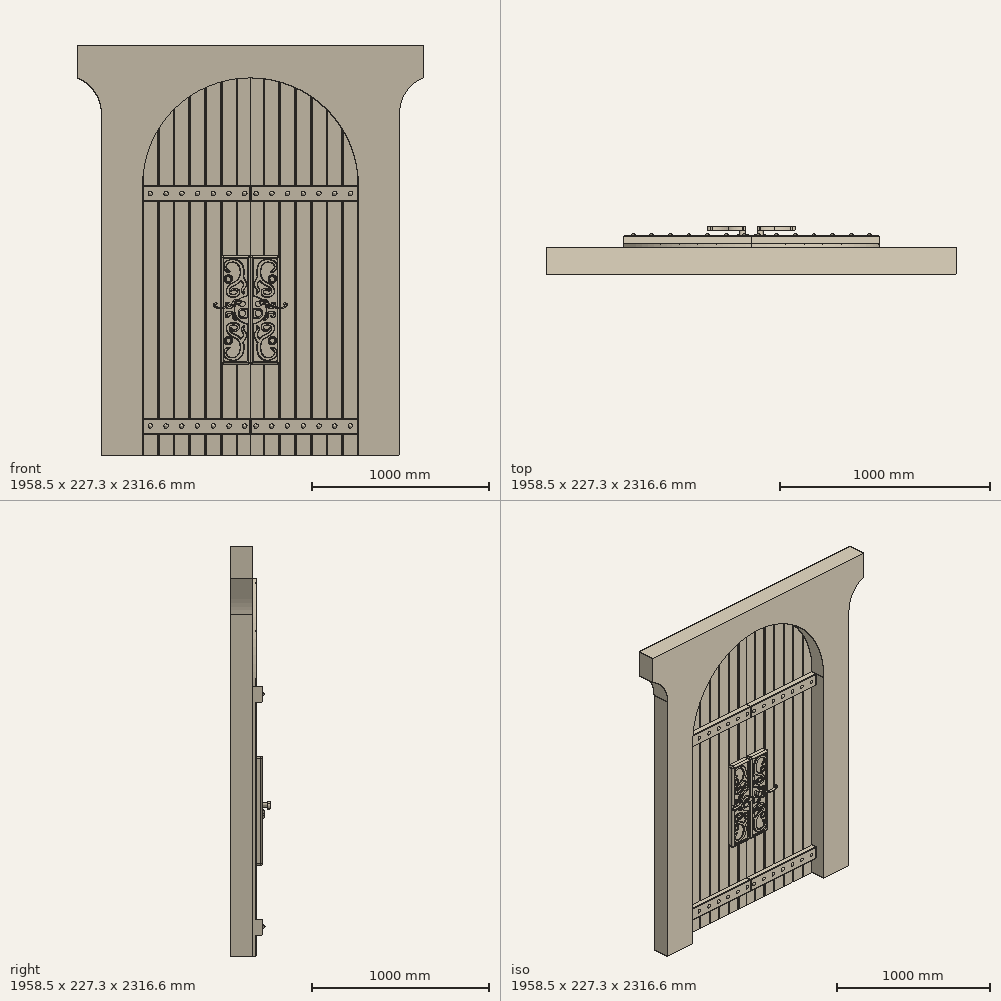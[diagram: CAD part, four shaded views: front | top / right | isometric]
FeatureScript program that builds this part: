
annotation { "Feature Type Name" : "Feature", "Feature Type Description" : "" }
export const myFeature = defineFeature(function(context is Context, id is Id, definition is map)
    precondition{}
    {
        {
            var Q0;
            Q0=qCreatedBy(makeId("Front.planeOp"),FACE);
            var sketch = newSketch(context, id + "F0", { "sketchPlane" : qUnion([Q0])});
            skLineSegment(sketch, "E0.bottom", {"start": v(0, 0) * mm, "end": v(609.6, 0) * mm});
            skLineSegment(sketch, "E0.left", {"start": v(0, 0) * mm, "end": v(0, 1524) * mm});
            skLineSegment(sketch, "E0.right", {"start": v(609.6, 0) * mm, "end": v(609.6, 2133.6) * mm});
            skArc(sketch, "E1", {"start": v(609.6, 2133.6) * mm, "mid": v(178.55, 1955.05) * mm, "end": v(0, 1524) * mm});
            skSolve(sketch);
        }
        {
            var Q0;
            Q0 = qSketchRegion(id + "F0", true);
            extrude(context, id + "F1", {"entities" : qUnion([Q0]), "depth" : 38.1 * mm, "offsetDistance" : 25.4 * mm});
        }
        {
            var Q0;
            Q0=makeQuery(id+"F1.opExtrude","SWEPT_FACE",FACE,{"disambiguationData":[OSD([sQuery(id+"F0.wireOp",EDGE,"E0.bottom")])]});
            var sketch = newSketch(context, id + "F2", { "sketchPlane" : qUnion([Q0])});
            skLineSegment(sketch, "E2.bottom", {"start": v(5.08, 38.1) * mm, "end": v(83.82, 38.1) * mm});
            skLineSegment(sketch, "E2.top", {"start": v(5.08, 0) * mm, "end": v(83.82, 0) * mm});
            skLineSegment(sketch, "E2.left", {"start": v(0, 33.02) * mm, "end": v(0, 5.08) * mm});
            skPoint(sketch, "E3.visualSharp", {"position": v(0, 38.1) * mm});
            skArc(sketch, "E3.filletArc", {"start": v(5.08, 38.1) * mm, "mid": v(1.49, 36.61) * mm, "end": v(0, 33.02) * mm});
            skPoint(sketch, "E4.visualSharp", {"position": v(0, 0) * mm});
            skArc(sketch, "E4.filletArc", {"start": v(0, 5.08) * mm, "mid": v(1.49, 1.49) * mm, "end": v(5.08, 0) * mm});
            skPoint(sketch, "E5.visualSharp", {"position": v(88.9, 0) * mm});
            skArc(sketch, "E5.filletArc", {"start": v(83.82, 0) * mm, "mid": v(87.41, 1.49) * mm, "end": v(88.9, 5.08) * mm});
            skPoint(sketch, "E6.visualSharp", {"position": v(88.9, 38.1) * mm});
            skArc(sketch, "E6.filletArc", {"start": v(88.9, 33.02) * mm, "mid": v(87.41, 36.61) * mm, "end": v(83.82, 38.1) * mm});
            skArc(sketch, "E7.1.0.0", {"start": v(177.8, 33.02) * mm, "mid": v(176.31, 36.61) * mm, "end": v(172.72, 38.1) * mm});
            skLineSegment(sketch, "E7.1.0.1", {"start": v(93.98, 38.1) * mm, "end": v(172.72, 38.1) * mm});
            skArc(sketch, "E7.1.0.3", {"start": v(172.72, 0) * mm, "mid": v(176.31, 1.49) * mm, "end": v(177.8, 5.08) * mm});
            skArc(sketch, "E7.1.0.4", {"start": v(88.9, 5.08) * mm, "mid": v(90.39, 1.49) * mm, "end": v(93.98, 0) * mm});
            skLineSegment(sketch, "E7.1.0.5", {"start": v(93.98, 0) * mm, "end": v(172.72, 0) * mm});
            skArc(sketch, "E7.1.0.7", {"start": v(93.98, 38.1) * mm, "mid": v(90.39, 36.61) * mm, "end": v(88.9, 33.02) * mm});
            skArc(sketch, "E7.2.0.0", {"start": v(266.7, 33.02) * mm, "mid": v(265.21, 36.61) * mm, "end": v(261.62, 38.1) * mm});
            skLineSegment(sketch, "E7.2.0.1", {"start": v(182.88, 38.1) * mm, "end": v(261.62, 38.1) * mm});
            skArc(sketch, "E7.2.0.3", {"start": v(261.62, 0) * mm, "mid": v(265.21, 1.49) * mm, "end": v(266.7, 5.08) * mm});
            skArc(sketch, "E7.2.0.4", {"start": v(177.8, 5.08) * mm, "mid": v(179.29, 1.49) * mm, "end": v(182.88, 0) * mm});
            skLineSegment(sketch, "E7.2.0.5", {"start": v(182.88, 0) * mm, "end": v(261.62, 0) * mm});
            skArc(sketch, "E7.2.0.7", {"start": v(182.88, 38.1) * mm, "mid": v(179.29, 36.61) * mm, "end": v(177.8, 33.02) * mm});
            skLineSegment(sketch, "E7.direction1", {"start": v(83.82, 33.02) * mm, "end": v(172.72, 33.02) * mm, "construction": true});
            skArc(sketch, "E8.0.3.0", {"start": v(355.6, 33.02) * mm, "mid": v(354.11, 36.61) * mm, "end": v(350.52, 38.1) * mm});
            skLineSegment(sketch, "E8.4.3.0", {"start": v(271.78, 38.1) * mm, "end": v(350.52, 38.1) * mm});
            skArc(sketch, "E8.10.3.0", {"start": v(350.52, 0) * mm, "mid": v(354.11, 1.49) * mm, "end": v(355.6, 5.08) * mm});
            skArc(sketch, "E8.14.3.0", {"start": v(266.7, 5.08) * mm, "mid": v(268.19, 1.49) * mm, "end": v(271.78, 0) * mm});
            skLineSegment(sketch, "E8.18.3.0", {"start": v(271.78, 0) * mm, "end": v(350.52, 0) * mm});
            skArc(sketch, "E8.24.3.0", {"start": v(271.78, 38.1) * mm, "mid": v(268.19, 36.61) * mm, "end": v(266.7, 33.02) * mm});
            skArc(sketch, "E8.0.4.0", {"start": v(444.5, 33.02) * mm, "mid": v(443.01, 36.61) * mm, "end": v(439.42, 38.1) * mm});
            skLineSegment(sketch, "E8.4.4.0", {"start": v(360.68, 38.1) * mm, "end": v(439.42, 38.1) * mm});
            skArc(sketch, "E8.10.4.0", {"start": v(439.42, 0) * mm, "mid": v(443.01, 1.49) * mm, "end": v(444.5, 5.08) * mm});
            skArc(sketch, "E8.14.4.0", {"start": v(355.6, 5.08) * mm, "mid": v(357.09, 1.49) * mm, "end": v(360.68, 0) * mm});
            skLineSegment(sketch, "E8.18.4.0", {"start": v(360.68, 0) * mm, "end": v(439.42, 0) * mm});
            skArc(sketch, "E8.24.4.0", {"start": v(360.68, 38.1) * mm, "mid": v(357.09, 36.61) * mm, "end": v(355.6, 33.02) * mm});
            skArc(sketch, "E8.0.5.0", {"start": v(533.4, 33.02) * mm, "mid": v(531.91, 36.61) * mm, "end": v(528.32, 38.1) * mm});
            skLineSegment(sketch, "E8.4.5.0", {"start": v(449.58, 38.1) * mm, "end": v(528.32, 38.1) * mm});
            skArc(sketch, "E8.10.5.0", {"start": v(528.32, 0) * mm, "mid": v(531.91, 1.49) * mm, "end": v(533.4, 5.08) * mm});
            skArc(sketch, "E8.14.5.0", {"start": v(444.5, 5.08) * mm, "mid": v(445.99, 1.49) * mm, "end": v(449.58, 0) * mm});
            skLineSegment(sketch, "E8.18.5.0", {"start": v(449.58, 0) * mm, "end": v(528.32, 0) * mm});
            skArc(sketch, "E8.24.5.0", {"start": v(449.58, 38.1) * mm, "mid": v(445.99, 36.61) * mm, "end": v(444.5, 33.02) * mm});
            skArc(sketch, "E8.0.6.0", {"start": v(622.3, 33.02) * mm, "mid": v(620.81, 36.61) * mm, "end": v(617.22, 38.1) * mm});
            skLineSegment(sketch, "E8.4.6.0", {"start": v(538.48, 38.1) * mm, "end": v(617.22, 38.1) * mm});
            skLineSegment(sketch, "E8.7.6.0", {"start": v(622.3, 33.02) * mm, "end": v(622.3, 5.08) * mm});
            skArc(sketch, "E8.10.6.0", {"start": v(617.22, 0) * mm, "mid": v(620.81, 1.49) * mm, "end": v(622.3, 5.08) * mm});
            skArc(sketch, "E8.14.6.0", {"start": v(533.4, 5.08) * mm, "mid": v(534.89, 1.49) * mm, "end": v(538.48, 0) * mm});
            skLineSegment(sketch, "E8.18.6.0", {"start": v(538.48, 0) * mm, "end": v(617.22, 0) * mm});
            skArc(sketch, "E8.24.6.0", {"start": v(538.48, 38.1) * mm, "mid": v(534.89, 36.61) * mm, "end": v(533.4, 33.02) * mm});
            skLineSegment(sketch, "E9.bottom", {"start": v(-46.54, 115.07) * mm, "end": v(633.76, 115.07) * mm});
            skLineSegment(sketch, "E9.top", {"start": v(-46.54, -46) * mm, "end": v(633.76, -46) * mm});
            skLineSegment(sketch, "E9.left", {"start": v(-46.54, 115.07) * mm, "end": v(-46.54, -46) * mm});
            skLineSegment(sketch, "E9.right", {"start": v(633.76, 115.07) * mm, "end": v(633.76, -46) * mm});
            skSolve(sketch);
        }
        {
            var Q0;
            Q0 = qSketchRegion(id + "F2", true);
            extrude(context, id + "F3", {"entities" : qUnion([Q0]), "operationType" : NewBodyOperationType.REMOVE, "oppositeDirection" : true, "depth" : 2153.92 * mm, "offsetDistance" : 25.4 * mm});
        }
        {
            var Q0;
            Q0=qCreatedBy(makeId("Front.planeOp"),FACE);
            cPlane(context, id + "F4", {"entities" : qUnion([Q0]), "cplaneType" : CPlaneType.OFFSET, "offset" : 19.05 * mm, "width" : 152.4 * mm, "height" : 152.4 * mm});
        }
        {
            var Q0;
            Q0=qCreatedBy(id+"F4.planeOp",FACE);
            var sketch = newSketch(context, id + "F5", { "sketchPlane" : qUnion([Q0])});
            skLineSegment(sketch, "E10.bottom", {"start": v(0, 1524) * mm, "end": v(609.6, 1524) * mm});
            skLineSegment(sketch, "E10.top", {"start": v(0, 1435.1) * mm, "end": v(609.6, 1435.1) * mm});
            skLineSegment(sketch, "E10.left", {"start": v(0, 1524) * mm, "end": v(0, 1435.1) * mm});
            skLineSegment(sketch, "E10.right", {"start": v(609.6, 1524) * mm, "end": v(609.6, 1435.1) * mm});
            skLineSegment(sketch, "E11.bottom", {"start": v(0, 120.72) * mm, "end": v(609.6, 120.72) * mm});
            skLineSegment(sketch, "E11.top", {"start": v(0, 209.62) * mm, "end": v(609.6, 209.62) * mm});
            skLineSegment(sketch, "E11.left", {"start": v(0, 120.72) * mm, "end": v(0, 209.62) * mm});
            skLineSegment(sketch, "E11.right", {"start": v(609.6, 120.72) * mm, "end": v(609.6, 209.62) * mm});
            skSolve(sketch);
        }
        {
            var Q0;
            Q0 = qSketchRegion(id + "F5", true);
            extrude(context, id + "F6", {"entities" : qUnion([Q0]), "operationType" : NewBodyOperationType.ADD, "depth" : 57.15 * mm, "offsetDistance" : 25.4 * mm, "hasSecondDirection" : true, "secondDirectionOppositeDirection" : true, "secondDirectionDepth" : 57.15 * mm});
        }
        {
            var Q0;
            Q0=makeQuery(id+"F6.opExtrude","CAP_EDGE",EDGE,{"disambiguationData":[OSD([sQuery(id+"F5.wireOp",EDGE,"E10.bottom")])],"isStart":false});
            var Q1;
            Q1=makeQuery(id+"F6.opExtrude","CAP_EDGE",EDGE,{"disambiguationData":[OSD([sQuery(id+"F5.wireOp",EDGE,"E10.top")])],"isStart":false});
            var Q2;
            Q2=makeQuery(id+"F6.opExtrude","CAP_EDGE",EDGE,{"disambiguationData":[OSD([sQuery(id+"F5.wireOp",EDGE,"E10.left")])],"isStart":false});
            var Q3;
            Q3=makeQuery(id+"F6.opExtrude","CAP_EDGE",EDGE,{"disambiguationData":[OSD([sQuery(id+"F5.wireOp",EDGE,"E10.right")])],"isStart":false});
            var Q4;
            Q4=makeQuery(id+"F6.opExtrude","CAP_FACE",FACE,{"disambiguationData":[OSD([sQuery(id+"F5.wireOp",EDGE,"E11.bottom"),sQuery(id+"F5.wireOp",EDGE,"E11.top"),sQuery(id+"F5.wireOp",EDGE,"E11.left"),sQuery(id+"F5.wireOp",EDGE,"E11.right")])],"isStart":false});
            var Q5;
            Q5=makeQuery(id+"F6.opExtrude","CAP_FACE",FACE,{"disambiguationData":[OSD([sQuery(id+"F5.wireOp",EDGE,"E10.bottom"),sQuery(id+"F5.wireOp",EDGE,"E10.top"),sQuery(id+"F5.wireOp",EDGE,"E10.left"),sQuery(id+"F5.wireOp",EDGE,"E10.right")])],"isStart":true});
            var Q6;
            Q6=makeQuery(id+"F6.opExtrude","CAP_FACE",FACE,{"disambiguationData":[OSD([sQuery(id+"F5.wireOp",EDGE,"E11.bottom"),sQuery(id+"F5.wireOp",EDGE,"E11.top"),sQuery(id+"F5.wireOp",EDGE,"E11.left"),sQuery(id+"F5.wireOp",EDGE,"E11.right")])],"isStart":true});
            fillet(context, id + "F7", {"entities" : qUnion([Q0, Q1, Q2, Q3, Q4, Q5, Q6]), "radius" : 5.08 * mm, "tangentPropagation" : true, "allowEdgeOverflow" : false});
        }
        {
            var Q0;
            Q0=qCreatedBy(id+"F4.planeOp",FACE);
            var sketch = newSketch(context, id + "F8", { "sketchPlane" : qUnion([Q0])});
            skLineSegment(sketch, "E12.bottom", {"start": v(609.6, 1130.3) * mm, "end": v(444.5, 1130.3) * mm});
            skLineSegment(sketch, "E12.top", {"start": v(609.6, 514.42) * mm, "end": v(444.5, 514.42) * mm});
            skLineSegment(sketch, "E12.left", {"start": v(609.6, 1130.3) * mm, "end": v(609.6, 514.42) * mm});
            skLineSegment(sketch, "E12.right", {"start": v(444.5, 1130.3) * mm, "end": v(444.5, 514.42) * mm});
            skSolve(sketch);
        }
        {
            var Q0;
            Q0 = qSketchRegion(id + "F8", true);
            extrude(context, id + "F9", {"entities" : qUnion([Q0]), "operationType" : NewBodyOperationType.ADD, "depth" : 57.15 * mm, "offsetDistance" : 25.4 * mm, "hasSecondDirection" : true, "secondDirectionOppositeDirection" : true, "secondDirectionDepth" : 57.15 * mm});
        }
        {
            var Q0;
            {var subQ0=sQuery(id+"F8.wireOp",EDGE,"E12.left");var subQ1=sQuery(id+"F8.wireOp",EDGE,"E12.bottom");var subQ2=sQuery(id+"F0.wireOp",EDGE,"E0.right");Q0=makeQuery(id+"F9.boolean.opBoolean","SPLIT",EDGE,{"disambiguationData":[TD([makeQuery(id+"F1.opExtrude","CAP_FACE",FACE,{"disambiguationData":[OSD([sQuery(id+"F0.wireOp",EDGE,"E0.bottom"),sQuery(id+"F0.wireOp",EDGE,"E0.left"),subQ2,sQuery(id+"F0.wireOp",EDGE,"E1")])],"isStart":false})])],"derivedFrom":makeQuery(id+"F9.opExtrude","SWEPT_EDGE",EDGE,{"disambiguationData":[OSD([subQ1,subQ0])]})});}
            var Q1;
            {var subQ0=sQuery(id+"F8.wireOp",EDGE,"E12.right");var subQ1=sQuery(id+"F8.wireOp",EDGE,"E12.bottom");Q1=makeQuery(id+"F9.boolean.opBoolean","SPLIT",EDGE,{"disambiguationData":[TD([makeQuery(id+"F3.boolean.opBoolean","COPY",FACE,{"derivedFrom":makeQuery(id+"F3.opExtrude","SWEPT_FACE",FACE,{"disambiguationData":[OSD([sQuery(id+"F2.wireOp",EDGE,"E8.0.4.0")])]})})])],"derivedFrom":makeQuery(id+"F9.opExtrude","SWEPT_EDGE",EDGE,{"disambiguationData":[OSD([subQ1,subQ0])]})});}
            var Q2;
            {var subQ0=sQuery(id+"F0.wireOp",EDGE,"E0.right");var subQ1=sQuery(id+"F8.wireOp",EDGE,"E12.bottom");var subQ2=sQuery(id+"F8.wireOp",EDGE,"E12.left");Q2=makeQuery(id+"F9.boolean.opBoolean","SPLIT",EDGE,{"disambiguationData":[TD([makeQuery(id+"F1.opExtrude","CAP_FACE",FACE,{"disambiguationData":[OSD([sQuery(id+"F0.wireOp",EDGE,"E0.bottom"),sQuery(id+"F0.wireOp",EDGE,"E0.left"),subQ0,sQuery(id+"F0.wireOp",EDGE,"E1")])],"isStart":true})])],"derivedFrom":makeQuery(id+"F9.opExtrude","SWEPT_EDGE",EDGE,{"disambiguationData":[OSD([subQ1,subQ2])]})});}
            var Q3;
            {var subQ0=sQuery(id+"F8.wireOp",EDGE,"E12.right");var subQ1=sQuery(id+"F8.wireOp",EDGE,"E12.bottom");Q3=makeQuery(id+"F9.boolean.opBoolean","SPLIT",EDGE,{"disambiguationData":[TD([makeQuery(id+"F3.boolean.opBoolean","COPY",FACE,{"derivedFrom":makeQuery(id+"F3.opExtrude","SWEPT_FACE",FACE,{"disambiguationData":[OSD([sQuery(id+"F2.wireOp",EDGE,"E8.10.4.0")])]})})])],"derivedFrom":makeQuery(id+"F9.opExtrude","SWEPT_EDGE",EDGE,{"disambiguationData":[OSD([subQ1,subQ0])]})});}
            var Q4;
            {var subQ0=sQuery(id+"F8.wireOp",EDGE,"E12.top");var subQ1=sQuery(id+"F8.wireOp",EDGE,"E12.right");Q4=makeQuery(id+"F9.boolean.opBoolean","SPLIT",EDGE,{"disambiguationData":[TD([makeQuery(id+"F3.boolean.opBoolean","COPY",FACE,{"derivedFrom":makeQuery(id+"F3.opExtrude","SWEPT_FACE",FACE,{"disambiguationData":[OSD([sQuery(id+"F2.wireOp",EDGE,"E8.10.4.0")])]})})])],"derivedFrom":makeQuery(id+"F9.opExtrude","SWEPT_EDGE",EDGE,{"disambiguationData":[OSD([subQ0,subQ1])]})});}
            var Q5;
            {var subQ0=sQuery(id+"F0.wireOp",EDGE,"E0.right");var subQ1=sQuery(id+"F8.wireOp",EDGE,"E12.top");var subQ2=sQuery(id+"F8.wireOp",EDGE,"E12.left");Q5=makeQuery(id+"F9.boolean.opBoolean","SPLIT",EDGE,{"disambiguationData":[TD([makeQuery(id+"F1.opExtrude","CAP_FACE",FACE,{"disambiguationData":[OSD([sQuery(id+"F0.wireOp",EDGE,"E0.bottom"),sQuery(id+"F0.wireOp",EDGE,"E0.left"),subQ0,sQuery(id+"F0.wireOp",EDGE,"E1")])],"isStart":true})])],"derivedFrom":makeQuery(id+"F9.opExtrude","SWEPT_EDGE",EDGE,{"disambiguationData":[OSD([subQ1,subQ2])]})});}
            var Q6;
            {var subQ0=sQuery(id+"F8.wireOp",EDGE,"E12.left");var subQ1=sQuery(id+"F8.wireOp",EDGE,"E12.top");var subQ2=sQuery(id+"F0.wireOp",EDGE,"E0.right");Q6=makeQuery(id+"F9.boolean.opBoolean","SPLIT",EDGE,{"disambiguationData":[TD([makeQuery(id+"F1.opExtrude","CAP_FACE",FACE,{"disambiguationData":[OSD([sQuery(id+"F0.wireOp",EDGE,"E0.bottom"),sQuery(id+"F0.wireOp",EDGE,"E0.left"),subQ2,sQuery(id+"F0.wireOp",EDGE,"E1")])],"isStart":false})])],"derivedFrom":makeQuery(id+"F9.opExtrude","SWEPT_EDGE",EDGE,{"disambiguationData":[OSD([subQ1,subQ0])]})});}
            var Q7;
            {var subQ0=sQuery(id+"F8.wireOp",EDGE,"E12.right");var subQ1=sQuery(id+"F8.wireOp",EDGE,"E12.top");Q7=makeQuery(id+"F9.boolean.opBoolean","SPLIT",EDGE,{"disambiguationData":[TD([makeQuery(id+"F3.boolean.opBoolean","COPY",FACE,{"derivedFrom":makeQuery(id+"F3.opExtrude","SWEPT_FACE",FACE,{"disambiguationData":[OSD([sQuery(id+"F2.wireOp",EDGE,"E8.0.4.0")])]})})])],"derivedFrom":makeQuery(id+"F9.opExtrude","SWEPT_EDGE",EDGE,{"disambiguationData":[OSD([subQ1,subQ0])]})});}
            var Q8;
            Q8=makeQuery(id+"F9.opExtrude","CAP_FACE",FACE,{"disambiguationData":[OSD([sQuery(id+"F8.wireOp",EDGE,"E12.bottom"),sQuery(id+"F8.wireOp",EDGE,"E12.top"),sQuery(id+"F8.wireOp",EDGE,"E12.left"),sQuery(id+"F8.wireOp",EDGE,"E12.right")])],"isStart":false});
            var Q9;
            Q9=makeQuery(id+"F9.opExtrude","CAP_FACE",FACE,{"disambiguationData":[OSD([sQuery(id+"F8.wireOp",EDGE,"E12.bottom"),sQuery(id+"F8.wireOp",EDGE,"E12.top"),sQuery(id+"F8.wireOp",EDGE,"E12.left"),sQuery(id+"F8.wireOp",EDGE,"E12.right")])],"isStart":true});
            fillet(context, id + "F10", {"entities" : qUnion([Q0, Q1, Q2, Q3, Q4, Q5, Q6, Q7, Q8, Q9]), "radius" : 12.7 * mm, "tangentPropagation" : true, "allowEdgeOverflow" : false});
        }
        {
            var Q0;
            Q0=makeQuery(id+"F9.opExtrude","CAP_FACE",FACE,{"disambiguationData":[OSD([sQuery(id+"F8.wireOp",EDGE,"E12.bottom"),sQuery(id+"F8.wireOp",EDGE,"E12.top"),sQuery(id+"F8.wireOp",EDGE,"E12.left"),sQuery(id+"F8.wireOp",EDGE,"E12.right")])],"isStart":false});
            var sketch = newSketch(context, id + "F11", { "sketchPlane" : qUnion([Q0])});
            skArc(sketch, "E13", {"start": v(586.01, 746.94) * mm, "mid": v(520.7, 822.36) * mm, "end": v(586.01, 897.78) * mm});
            skLineSegment(sketch, "E14", {"start": v(596.9, 734.37) * mm, "end": v(596.9, 539.82) * mm});
            skLineSegment(sketch, "E15", {"start": v(584.2, 527.12) * mm, "end": v(469.9, 527.12) * mm});
            skLineSegment(sketch, "E16", {"start": v(457.2, 539.82) * mm, "end": v(457.2, 1104.9) * mm});
            skLineSegment(sketch, "E17", {"start": v(469.9, 1117.6) * mm, "end": v(584.2, 1117.6) * mm});
            skLineSegment(sketch, "E18", {"start": v(596.9, 1104.9) * mm, "end": v(596.9, 910.35) * mm});
            skPoint(sketch, "E19.visualSharp", {"position": v(596.9, 1117.6) * mm});
            skArc(sketch, "E19.filletArc", {"start": v(596.9, 1104.9) * mm, "mid": v(593.18, 1113.88) * mm, "end": v(584.2, 1117.6) * mm});
            skPoint(sketch, "E20.visualSharp", {"position": v(457.2, 1117.6) * mm});
            skArc(sketch, "E20.filletArc", {"start": v(469.9, 1117.6) * mm, "mid": v(460.92, 1113.88) * mm, "end": v(457.2, 1104.9) * mm});
            skPoint(sketch, "E21.visualSharp", {"position": v(457.2, 527.12) * mm});
            skArc(sketch, "E21.filletArc", {"start": v(457.2, 539.82) * mm, "mid": v(460.92, 530.84) * mm, "end": v(469.9, 527.12) * mm});
            skPoint(sketch, "E22.visualSharp", {"position": v(596.9, 527.12) * mm});
            skArc(sketch, "E22.filletArc", {"start": v(584.2, 527.12) * mm, "mid": v(593.18, 530.84) * mm, "end": v(596.9, 539.82) * mm});
            skPoint(sketch, "E23.visualSharp", {"position": v(596.9, 746.16) * mm});
            skArc(sketch, "E23.filletArc", {"start": v(596.9, 734.37) * mm, "mid": v(593.8, 742.69) * mm, "end": v(586.01, 746.94) * mm});
            skPoint(sketch, "E24.visualSharp", {"position": v(596.9, 898.56) * mm});
            skArc(sketch, "E24.filletArc", {"start": v(586.01, 897.78) * mm, "mid": v(593.8, 902.03) * mm, "end": v(596.9, 910.35) * mm});
            skSolve(sketch);
        }
        {
            var Q0;
            Q0 = qSketchRegion(id + "F11", true);
            extrude(context, id + "F12", {"entities" : qUnion([Q0]), "operationType" : NewBodyOperationType.REMOVE, "oppositeDirection" : true, "depth" : 12.7 * mm, "offsetDistance" : 25.4 * mm});
        }
        {
            var Q0;
            Q0=makeQuery(id+"F12.boolean.opBoolean","COPY",FACE,{"derivedFrom":makeQuery(id+"F12.opExtrude","CAP_FACE",FACE,{"disambiguationData":[OSD([sQuery(id+"F11.wireOp",EDGE,"E13"),sQuery(id+"F11.wireOp",EDGE,"E14"),sQuery(id+"F11.wireOp",EDGE,"E15"),sQuery(id+"F11.wireOp",EDGE,"E16"),sQuery(id+"F11.wireOp",EDGE,"E17"),sQuery(id+"F11.wireOp",EDGE,"E18"),sQuery(id+"F11.wireOp",EDGE,"E19.filletArc"),sQuery(id+"F11.wireOp",EDGE,"E20.filletArc"),sQuery(id+"F11.wireOp",EDGE,"E21.filletArc"),sQuery(id+"F11.wireOp",EDGE,"E22.filletArc"),sQuery(id+"F11.wireOp",EDGE,"E23.filletArc"),sQuery(id+"F11.wireOp",EDGE,"E24.filletArc")])],"isStart":false})});
            var sketch = newSketch(context, id + "F13", { "sketchPlane" : qUnion([Q0])});
            skFitSpline(sketch, "E25", {"points": [v(492.7, 1037.53) * mm, v(474.58, 1054) * mm, v(476.78, 1080.37) * mm, v(499.85, 1092.45) * mm, v(527.3, 1090.26) * mm, v(544.88, 1071.58) * mm, v(553.12, 1046.87) * mm, v(553.12, 1020.5) * mm, v(548.18, 1004.03) * mm, v(537.74, 989.75) * mm, v(513.58, 974.37) * mm, v(486.12, 954.6) * mm, v(476.23, 932.08) * mm, v(478.43, 912.3) * mm, v(492.7, 900.22) * mm, v(522.91, 896.93) * mm, v(544.33, 909.56) * mm, v(545.43, 929.33) * mm, v(530.6, 941.96) * mm, v(506.44, 938.12) * mm, v(498.2, 926.59) * mm, v(509.73, 934.28) * mm, v(523.46, 936.47) * mm, v(535.55, 927.68) * mm, v(536.1, 916.7) * mm, v(524.56, 908.46) * mm, v(504.24, 908.46) * mm, v(490.5, 917.8) * mm, v(489.41, 931.53) * mm, v(496, 944.71) * mm, v(511.38, 956.8) * mm, v(535.55, 969.97) * mm, v(555.87, 988.1) * mm, v(567.4, 1008.97) * mm, v(571.8, 1028.74) * mm, v(569.05, 1058.4) * mm, v(556.42, 1086.41) * mm, v(534.45, 1102.34) * mm, v(512.48, 1106.18) * mm, v(486.66, 1101.24) * mm, v(471.84, 1091.9) * mm, v(461.95, 1077.07) * mm, v(462.5, 1055.65) * mm, v(476.23, 1039.73) * mm, v(492.7, 1037.53) * mm]});
            skFitSpline(sketch, "E26", {"points": [v(555.87, 988.1) * mm, v(569.05, 974.37) * mm, v(572.9, 960.64) * mm, v(565.75, 945.8) * mm, v(559.71, 932.08) * mm, v(574, 911.2) * mm, v(569.6, 928.78) * mm, v(573.44, 939.22) * mm, v(584.98, 954.05) * mm, v(586.62, 969.97) * mm, v(580.58, 983.7) * mm, v(567.4, 1008.97) * mm], "startDerivative": vector(157.67, -139.92) * mm, "endDerivative": vector(-122.09, 237.54) * mm});
            skFitSpline(sketch, "E27.MirrorCS", {"points": [v(555.87, 656.62) * mm, v(569.05, 670.35) * mm, v(572.9, 684.08) * mm, v(565.75, 698.91) * mm, v(559.71, 712.64) * mm, v(574, 733.51) * mm, v(569.6, 715.94) * mm, v(573.44, 705.5) * mm, v(584.98, 690.67) * mm, v(586.62, 674.75) * mm, v(580.58, 661.01) * mm, v(567.4, 635.75) * mm], "startDerivative": vector(157.67, 139.92) * mm, "endDerivative": vector(-122.09, -237.54) * mm});
            skFitSpline(sketch, "E28.MirrorCS", {"points": [v(492.7, 607.2) * mm, v(474.58, 590.71) * mm, v(476.78, 564.35) * mm, v(499.85, 552.27) * mm, v(527.3, 554.47) * mm, v(544.88, 573.14) * mm, v(553.12, 597.85) * mm, v(553.12, 624.22) * mm, v(548.18, 640.7) * mm, v(537.74, 654.97) * mm, v(513.58, 670.35) * mm, v(486.12, 690.12) * mm, v(476.23, 712.64) * mm, v(478.43, 732.41) * mm, v(492.7, 744.5) * mm, v(522.91, 747.8) * mm, v(544.33, 735.16) * mm, v(545.43, 715.39) * mm, v(530.6, 702.76) * mm, v(506.44, 706.6) * mm, v(498.2, 718.13) * mm, v(509.73, 710.44) * mm, v(523.46, 708.25) * mm, v(535.55, 717.04) * mm, v(536.1, 728.02) * mm, v(524.56, 736.26) * mm, v(504.24, 736.26) * mm, v(490.5, 726.92) * mm, v(489.41, 713.2) * mm, v(496, 700) * mm, v(511.38, 687.93) * mm, v(535.55, 674.75) * mm, v(555.87, 656.62) * mm, v(567.4, 635.75) * mm, v(571.8, 615.98) * mm, v(569.05, 586.32) * mm, v(556.42, 558.3) * mm, v(534.45, 542.38) * mm, v(512.48, 538.54) * mm, v(486.66, 543.48) * mm, v(471.84, 552.82) * mm, v(461.95, 567.65) * mm, v(462.5, 589.07) * mm, v(476.23, 605) * mm, v(492.7, 607.2) * mm]});
            skPoint(sketch, "E29.start.orphan", {"position": v(596.9, 822.36) * mm});
            skFitSpline(sketch, "E30", {"points": [v(493.45, 858.5) * mm, v(486.1, 861.6) * mm, v(478.1, 858.02) * mm, v(475.98, 850.02) * mm, v(479.25, 843) * mm, v(490.02, 839.73) * mm, v(500.15, 841.69) * mm, v(508.47, 850.83) * mm, v(511.74, 864.06) * mm, v(517.94, 875.98) * mm, v(528.72, 880.22) * mm, v(537.54, 877.12) * mm, v(542.76, 869.12) * mm, v(551.74, 846.75) * mm, v(541.13, 862.26) * mm, v(534.44, 871.57) * mm, v(528.23, 872.39) * mm, v(522.19, 867.32) * mm, v(519.74, 856.71) * mm, v(510.92, 837.93) * mm, v(491.82, 831.57) * mm, v(474.35, 837.93) * mm, v(468.96, 851.49) * mm, v(473.37, 861.6) * mm, v(482.51, 864.55) * mm, v(493.45, 858.5) * mm]});
            skFitSpline(sketch, "E31.MirrorC", {"points": [v(493.45, 786.21) * mm, v(486.1, 783.11) * mm, v(478.1, 786.7) * mm, v(475.98, 794.7) * mm, v(479.25, 801.73) * mm, v(490.02, 805) * mm, v(500.15, 803.03) * mm, v(508.47, 793.89) * mm, v(511.74, 780.66) * mm, v(517.94, 768.74) * mm, v(528.72, 764.5) * mm, v(537.54, 767.6) * mm, v(542.76, 775.6) * mm, v(551.74, 797.97) * mm, v(541.13, 782.46) * mm, v(534.44, 773.15) * mm, v(528.23, 772.33) * mm, v(522.19, 777.4) * mm, v(519.74, 788) * mm, v(510.92, 806.79) * mm, v(491.82, 813.16) * mm, v(474.35, 806.79) * mm, v(468.96, 793.23) * mm, v(473.37, 783.11) * mm, v(482.51, 780.17) * mm, v(493.45, 786.21) * mm]});
            skPoint(sketch, "E32.end.orphan", {"position": v(457.2, 822.36) * mm});
            skPoint(sketch, "E32.start.orphan", {"position": v(520.7, 822.36) * mm});
            skCircle(sketch, "E33", {"center": v(485.78, 648.46) * mm, "radius": 21.45 * mm});
            skCircle(sketch, "E34", {"center": v(485.78, 648.46) * mm, "radius": 14.27 * mm});
            skCircle(sketch, "E35.MirrorC", {"center": v(485.78, 996.26) * mm, "radius": 21.45 * mm});
            skCircle(sketch, "E36.MirrorC", {"center": v(485.78, 996.26) * mm, "radius": 14.27 * mm});
            skSolve(sketch);
        }
        {
            var Q0;
            Q0 = qSketchRegion(id + "F13", true);
            extrude(context, id + "F14", {"entities" : qUnion([Q0]), "operationType" : NewBodyOperationType.ADD, "depth" : 7.87 * mm, "offsetDistance" : 25.4 * mm});
        }
        {
            var Q0;
            {var subQ0=sQuery(id+"F11.wireOp",EDGE,"E22.filletArc");var subQ1=sQuery(id+"F11.wireOp",EDGE,"E21.filletArc");var subQ2=sQuery(id+"F11.wireOp",EDGE,"E20.filletArc");var subQ3=sQuery(id+"F11.wireOp",EDGE,"E19.filletArc");var subQ4=sQuery(id+"F11.wireOp",EDGE,"E18");var subQ5=sQuery(id+"F11.wireOp",EDGE,"E17");var subQ6=sQuery(id+"F11.wireOp",EDGE,"E13");var subQ7=sQuery(id+"F11.wireOp",EDGE,"E14");var subQ8=sQuery(id+"F11.wireOp",EDGE,"E15");var subQ9=sQuery(id+"F11.wireOp",EDGE,"E16");var subQ10=sQuery(id+"F11.wireOp",EDGE,"E23.filletArc");var subQ11=sQuery(id+"F11.wireOp",EDGE,"E24.filletArc");Q0=makeQuery(id+"F14.boolean.opBoolean","SPLIT",FACE,{"disambiguationData":[TD([makeQuery(id+"F12.boolean.opBoolean","COPY",FACE,{"derivedFrom":makeQuery(id+"F12.opExtrude","SWEPT_FACE",FACE,{"disambiguationData":[OSD([subQ6])]})})])],"derivedFrom":makeQuery(id+"F12.boolean.opBoolean","COPY",FACE,{"derivedFrom":makeQuery(id+"F12.opExtrude","CAP_FACE",FACE,{"disambiguationData":[OSD([subQ6,subQ7,subQ8,subQ9,subQ5,subQ4,subQ3,subQ2,subQ1,subQ0,subQ10,subQ11])],"isStart":false})})});}
            var Q1;
            Q1=makeQuery(id+"F14.opExtrude","CAP_EDGE",EDGE,{"disambiguationData":[OSD([sQuery(id+"F13.wireOp",EDGE,"E34")])],"isStart":false});
            var Q2;
            Q2=makeQuery(id+"F14.opExtrude","CAP_EDGE",EDGE,{"disambiguationData":[OSD([sQuery(id+"F13.wireOp",EDGE,"E36.MirrorC")])],"isStart":false});
            fillet(context, id + "F15", {"entities" : qUnion([Q0, Q1, Q2]), "radius" : 2.54 * mm, "tangentPropagation" : true, "allowEdgeOverflow" : false});
        }
        {
            var Q0;
            Q0=makeQuery(id+"F14.opExtrude","CAP_EDGE",EDGE,{"disambiguationData":[OSD([sQuery(id+"F13.wireOp",EDGE,"E35.MirrorC")])],"isStart":false});
            var Q1;
            Q1=makeQuery(id+"F14.opExtrude","CAP_EDGE",EDGE,{"disambiguationData":[OSD([sQuery(id+"F13.wireOp",EDGE,"E33")])],"isStart":false});
            chamfer(context, id + "F16", {"entities" : qUnion([Q0, Q1]), "width" : 2.54 * mm, "tangentPropagation" : true});
        }
        {
            var Q0;
            Q0=makeQuery(id+"F14.boolean.opBoolean","INTERSECT",EDGE,{"derivedFrom":[makeQuery(id+"F12.boolean.opBoolean","COPY",FACE,{"derivedFrom":makeQuery(id+"F12.opExtrude","SWEPT_FACE",FACE,{"disambiguationData":[OSD([sQuery(id+"F11.wireOp",EDGE,"E13")])]})}),makeQuery(id+"F14.opExtrude","CAP_FACE",FACE,{"disambiguationData":[OSD([sQuery(id+"F13.wireOp",EDGE,"E31.MirrorC")])],"isStart":false})]});
            var Q1;
            Q1=makeQuery(id+"F14.boolean.opBoolean","INTERSECT",EDGE,{"derivedFrom":[makeQuery(id+"F12.boolean.opBoolean","COPY",FACE,{"derivedFrom":makeQuery(id+"F12.opExtrude","SWEPT_FACE",FACE,{"disambiguationData":[OSD([sQuery(id+"F11.wireOp",EDGE,"E13")])]})}),makeQuery(id+"F14.opExtrude","CAP_FACE",FACE,{"disambiguationData":[OSD([sQuery(id+"F13.wireOp",EDGE,"E30")])],"isStart":false})]});
            fillet(context, id + "F17", {"entities" : qUnion([Q0, Q1]), "radius" : 20.32 * mm, "tangentPropagation" : true, "allowEdgeOverflow" : false});
        }
        {
            var Q0;
            Q0=makeQuery(id+"F6.opExtrude","CAP_FACE",FACE,{"disambiguationData":[OSD([sQuery(id+"F5.wireOp",EDGE,"E10.bottom"),sQuery(id+"F5.wireOp",EDGE,"E10.top"),sQuery(id+"F5.wireOp",EDGE,"E10.left"),sQuery(id+"F5.wireOp",EDGE,"E10.right")])],"isStart":false});
            var sketch = newSketch(context, id + "F18", { "sketchPlane" : qUnion([Q0])});
            skCircle(sketch, "E37", {"center": v(44.45, 165.92) * mm, "radius": 12.7 * mm});
            skCircle(sketch, "E38.1.0.0", {"center": v(133.35, 165.92) * mm, "radius": 12.7 * mm});
            skCircle(sketch, "E38.2.0.0", {"center": v(222.25, 165.92) * mm, "radius": 12.7 * mm});
            skLineSegment(sketch, "E38.direction1", {"start": v(44.45, 165.92) * mm, "end": v(133.35, 165.92) * mm, "construction": true});
            skCircle(sketch, "E39.0.3.0", {"center": v(311.15, 165.92) * mm, "radius": 12.7 * mm});
            skCircle(sketch, "E39.0.4.0", {"center": v(400.05, 165.92) * mm, "radius": 12.7 * mm});
            skCircle(sketch, "E39.0.5.0", {"center": v(488.95, 165.92) * mm, "radius": 12.7 * mm});
            skCircle(sketch, "E39.0.6.0", {"center": v(577.85, 165.92) * mm, "radius": 12.7 * mm});
            skCircle(sketch, "E40.1.0.0", {"center": v(44.45, 1479.1) * mm, "radius": 12.7 * mm});
            skCircle(sketch, "E40.1.0.1", {"center": v(133.35, 1479.1) * mm, "radius": 12.7 * mm});
            skCircle(sketch, "E40.1.0.2", {"center": v(222.25, 1479.1) * mm, "radius": 12.7 * mm});
            skCircle(sketch, "E40.1.0.3", {"center": v(311.15, 1479.1) * mm, "radius": 12.7 * mm});
            skCircle(sketch, "E40.1.0.4", {"center": v(400.05, 1479.1) * mm, "radius": 12.7 * mm});
            skCircle(sketch, "E40.1.0.5", {"center": v(488.95, 1479.1) * mm, "radius": 12.7 * mm});
            skCircle(sketch, "E40.1.0.6", {"center": v(577.85, 1479.1) * mm, "radius": 12.7 * mm});
            skLineSegment(sketch, "E40.direction1", {"start": v(44.45, 165.92) * mm, "end": v(44.45, 1479.1) * mm, "construction": true});
            skSolve(sketch);
        }
        {
            var Q0;
            Q0 = qSketchRegion(id + "F18", true);
            extrude(context, id + "F19", {"entities" : qUnion([Q0]), "operationType" : NewBodyOperationType.ADD, "depth" : 12.7 * mm, "offsetDistance" : 25.4 * mm});
        }
        {
            var Q0;
            Q0=makeQuery(id+"F19.opExtrude","CAP_EDGE",EDGE,{"disambiguationData":[OSD([sQuery(id+"F18.wireOp",EDGE,"E37")])],"isStart":false});
            var Q1;
            Q1=makeQuery(id+"F19.opExtrude","CAP_EDGE",EDGE,{"disambiguationData":[OSD([sQuery(id+"F18.wireOp",EDGE,"E38.1.0.0")])],"isStart":false});
            var Q2;
            Q2=makeQuery(id+"F19.opExtrude","CAP_EDGE",EDGE,{"disambiguationData":[OSD([sQuery(id+"F18.wireOp",EDGE,"E38.2.0.0")])],"isStart":false});
            var Q3;
            Q3=makeQuery(id+"F19.opExtrude","CAP_EDGE",EDGE,{"disambiguationData":[OSD([sQuery(id+"F18.wireOp",EDGE,"E39.0.3.0")])],"isStart":false});
            var Q4;
            Q4=makeQuery(id+"F19.opExtrude","CAP_EDGE",EDGE,{"disambiguationData":[OSD([sQuery(id+"F18.wireOp",EDGE,"E39.0.4.0")])],"isStart":false});
            var Q5;
            Q5=makeQuery(id+"F19.opExtrude","CAP_EDGE",EDGE,{"disambiguationData":[OSD([sQuery(id+"F18.wireOp",EDGE,"E39.0.5.0")])],"isStart":false});
            var Q6;
            Q6=makeQuery(id+"F19.opExtrude","CAP_EDGE",EDGE,{"disambiguationData":[OSD([sQuery(id+"F18.wireOp",EDGE,"E39.0.6.0")])],"isStart":false});
            var Q7;
            Q7=makeQuery(id+"F19.opExtrude","CAP_EDGE",EDGE,{"disambiguationData":[OSD([sQuery(id+"F18.wireOp",EDGE,"E40.1.0.0")])],"isStart":false});
            var Q8;
            Q8=makeQuery(id+"F19.opExtrude","CAP_EDGE",EDGE,{"disambiguationData":[OSD([sQuery(id+"F18.wireOp",EDGE,"E40.1.0.1")])],"isStart":false});
            var Q9;
            Q9=makeQuery(id+"F19.opExtrude","CAP_EDGE",EDGE,{"disambiguationData":[OSD([sQuery(id+"F18.wireOp",EDGE,"E40.1.0.2")])],"isStart":false});
            var Q10;
            Q10=makeQuery(id+"F19.opExtrude","CAP_EDGE",EDGE,{"disambiguationData":[OSD([sQuery(id+"F18.wireOp",EDGE,"E40.1.0.3")])],"isStart":false});
            var Q11;
            Q11=makeQuery(id+"F19.opExtrude","CAP_EDGE",EDGE,{"disambiguationData":[OSD([sQuery(id+"F18.wireOp",EDGE,"E40.1.0.4")])],"isStart":false});
            var Q12;
            Q12=makeQuery(id+"F19.opExtrude","CAP_EDGE",EDGE,{"disambiguationData":[OSD([sQuery(id+"F18.wireOp",EDGE,"E40.1.0.5")])],"isStart":false});
            var Q13;
            Q13=makeQuery(id+"F19.opExtrude","CAP_EDGE",EDGE,{"disambiguationData":[OSD([sQuery(id+"F18.wireOp",EDGE,"E40.1.0.6")])],"isStart":false});
            chamfer(context, id + "F20", {"entities" : qUnion([Q0, Q1, Q2, Q3, Q4, Q5, Q6, Q7, Q8, Q9, Q10, Q11, Q12, Q13]), "width" : 12.7 * mm, "tangentPropagation" : true});
        }
        {
            var Q0;
            {var subQ0=sQuery(id+"F8.wireOp",EDGE,"E12.left");Q0=makeQuery(id+"F12.boolean.opBoolean","SPLIT",FACE,{"disambiguationData":[TD([makeQuery(id+"F12.opExtrude","SWEPT_FACE",FACE,{"disambiguationData":[OSD([sQuery(id+"F11.wireOp",EDGE,"E13")])]})])],"derivedFrom":makeQuery(id+"F9.opExtrude","CAP_FACE",FACE,{"disambiguationData":[OSD([sQuery(id+"F8.wireOp",EDGE,"E12.bottom"),sQuery(id+"F8.wireOp",EDGE,"E12.top"),subQ0,sQuery(id+"F8.wireOp",EDGE,"E12.right")])],"isStart":false})});}
            var sketch = newSketch(context, id + "F21", { "sketchPlane" : qUnion([Q0])});
            skCircle(sketch, "E41", {"center": v(567.32, 855.41) * mm, "radius": 12.7 * mm});
            skSolve(sketch);
        }
        {
            var Q0;
            Q0 = qSketchRegion(id + "F21", true);
            extrude(context, id + "F22", {"entities" : qUnion([Q0]), "operationType" : NewBodyOperationType.ADD, "depth" : 25.4 * mm, "offsetDistance" : 25.4 * mm});
        }
        {
            var Q0;
            Q0=makeQuery(id+"F22.opExtrude","CAP_FACE",FACE,{"disambiguationData":[OSD([sQuery(id+"F21.wireOp",EDGE,"E41")])],"isStart":false});
            var sketch = newSketch(context, id + "F23", { "sketchPlane" : qUnion([Q0])});
            skArc(sketch, "E42", {"start": v(559.23, 842.5) * mm, "mid": v(581.66, 850.24) * mm, "end": v(569.34, 870.52) * mm});
            skArc(sketch, "E43", {"start": v(564.69, 871.6) * mm, "mid": v(530.76, 873.15) * mm, "end": v(501.04, 856.7) * mm});
            skArc(sketch, "E44", {"start": v(411.22, 841.87) * mm, "mid": v(455.95, 837.46) * mm, "end": v(497.76, 853.95) * mm});
            skArc(sketch, "E45", {"start": v(407.58, 850.9) * mm, "mid": v(407.62, 845.66) * mm, "end": v(411.22, 841.87) * mm});
            skArc(sketch, "E46.0", {"start": v(415.96, 861.71) * mm, "mid": v(401.24, 851.9) * mm, "end": v(408.87, 835.96) * mm});
            skArc(sketch, "E46.1", {"start": v(408.87, 835.96) * mm, "mid": v(455.92, 831.05) * mm, "end": v(500.13, 847.87) * mm});
            skArc(sketch, "E46.2", {"start": v(552.94, 867.87) * mm, "mid": v(537.8, 867.98) * mm, "end": v(523.19, 864.03) * mm});
            skArc(sketch, "E47", {"start": v(558.51, 842.93) * mm, "mid": v(535.29, 851.57) * mm, "end": v(510.51, 851.97) * mm});
            skArc(sketch, "E48.0", {"start": v(548.73, 854.47) * mm, "mid": v(536.6, 857.79) * mm, "end": v(524.1, 859.15) * mm});
            skArc(sketch, "E49.trimOffspring", {"start": v(554.68, 863.94) * mm, "mid": v(552.94, 860.46) * mm, "end": v(552.13, 856.65) * mm});
            skPoint(sketch, "E50.visualSharp", {"position": v(557.46, 867.04) * mm});
            skArc(sketch, "E50.filletArc", {"start": v(554.68, 863.94) * mm, "mid": v(554.9, 866.39) * mm, "end": v(552.94, 867.87) * mm});
            skPoint(sketch, "E51.visualSharp", {"position": v(552.25, 853.1) * mm});
            skArc(sketch, "E51.filletArc", {"start": v(548.73, 854.47) * mm, "mid": v(550.97, 854.72) * mm, "end": v(552.13, 856.65) * mm});
            skPoint(sketch, "E52.visualSharp", {"position": v(513.48, 858.76) * mm});
            skArc(sketch, "E52.filletArc", {"start": v(523.19, 864.03) * mm, "mid": v(521.68, 861.22) * mm, "end": v(524.1, 859.15) * mm});
            skPoint(sketch, "E53.visualSharp", {"position": v(504.02, 850.65) * mm});
            skArc(sketch, "E53.filletArc", {"start": v(510.51, 851.97) * mm, "mid": v(505.1, 850.5) * mm, "end": v(500.13, 847.87) * mm});
            skPoint(sketch, "E54.visualSharp", {"position": v(559, 842.64) * mm});
            skArc(sketch, "E54.filletArc", {"start": v(559.23, 842.5) * mm, "mid": v(558.87, 842.71) * mm, "end": v(558.51, 842.93) * mm});
            skPoint(sketch, "E55.visualSharp", {"position": v(499.78, 855.41) * mm});
            skArc(sketch, "E55.filletArc", {"start": v(497.76, 853.95) * mm, "mid": v(499.46, 855.26) * mm, "end": v(501.04, 856.7) * mm});
            skPoint(sketch, "E56.visualSharp", {"position": v(567.32, 870.65) * mm});
            skArc(sketch, "E56.filletArc", {"start": v(564.69, 871.6) * mm, "mid": v(567, 870.95) * mm, "end": v(569.34, 870.52) * mm});
            skArc(sketch, "E57", {"start": v(410.25, 851.37) * mm, "mid": v(420.7, 852.34) * mm, "end": v(415.96, 861.71) * mm});
            skArc(sketch, "E58", {"start": v(410.25, 851.37) * mm, "mid": v(408.8, 851.8) * mm, "end": v(407.58, 850.9) * mm});
            skSolve(sketch);
        }
        {
            var Q0;
            Q0 = qSketchRegion(id + "F23", true);
            extrude(context, id + "F24", {"entities" : qUnion([Q0]), "operationType" : NewBodyOperationType.ADD, "depth" : 17.78 * mm, "offsetDistance" : 25.4 * mm});
        }
        {
            var Q0;
            Q0=makeQuery(id+"F24.opExtrude","CAP_EDGE",EDGE,{"disambiguationData":[OSD([sQuery(id+"F23.wireOp",EDGE,"E48.0")])],"isStart":false});
            var Q1;
            Q1=makeQuery(id+"F24.opExtrude","CAP_EDGE",EDGE,{"disambiguationData":[OSD([sQuery(id+"F23.wireOp",EDGE,"E48.0")])],"isStart":true});
            fillet(context, id + "F25", {"entities" : qUnion([Q0, Q1]), "radius" : 2.54 * mm, "tangentPropagation" : true, "allowEdgeOverflow" : false});
        }
        {
            var Q0;
            {var subQ0=sQuery(id+"F8.wireOp",EDGE,"E12.left");Q0=makeQuery(id+"F12.boolean.opBoolean","SPLIT",FACE,{"disambiguationData":[TD([makeQuery(id+"F12.opExtrude","SWEPT_FACE",FACE,{"disambiguationData":[OSD([sQuery(id+"F11.wireOp",EDGE,"E13")])]})])],"derivedFrom":makeQuery(id+"F9.opExtrude","CAP_FACE",FACE,{"disambiguationData":[OSD([sQuery(id+"F8.wireOp",EDGE,"E12.bottom"),sQuery(id+"F8.wireOp",EDGE,"E12.top"),subQ0,sQuery(id+"F8.wireOp",EDGE,"E12.right")])],"isStart":false})});}
            var sketch = newSketch(context, id + "F26", { "sketchPlane" : qUnion([Q0])});
            skLineSegment(sketch, "E59.bottom", {"start": v(565.83, 831.9) * mm, "end": v(594.26, 831.9) * mm});
            skLineSegment(sketch, "E59.top", {"start": v(565.83, 772.59) * mm, "end": v(594.26, 772.59) * mm});
            skLineSegment(sketch, "E59.left", {"start": v(540.43, 806.5) * mm, "end": v(540.43, 797.99) * mm});
            skLineSegment(sketch, "E59.right", {"start": v(594.26, 831.9) * mm, "end": v(594.26, 772.59) * mm});
            skPoint(sketch, "E60.visualSharp", {"position": v(540.43, 772.59) * mm});
            skArc(sketch, "E60.filletArc", {"start": v(540.43, 797.99) * mm, "mid": v(547.87, 780.03) * mm, "end": v(565.83, 772.59) * mm});
            skPoint(sketch, "E61.visualSharp", {"position": v(540.43, 831.9) * mm});
            skArc(sketch, "E61.filletArc", {"start": v(565.83, 831.9) * mm, "mid": v(547.87, 824.47) * mm, "end": v(540.43, 806.5) * mm});
            skSolve(sketch);
        }
        {
            var Q0;
            Q0 = qSketchRegion(id + "F26", true);
            extrude(context, id + "F27", {"entities" : qUnion([Q0]), "operationType" : NewBodyOperationType.ADD, "depth" : 6.35 * mm, "offsetDistance" : 25.4 * mm});
        }
        {
            var Q0;
            Q0=makeQuery(id+"F27.opExtrude","CAP_EDGE",EDGE,{"disambiguationData":[OSD([sQuery(id+"F26.wireOp",EDGE,"E59.bottom")])],"isStart":false});
            chamfer(context, id + "F28", {"entities" : qUnion([Q0]), "width" : 7.62 * mm, "tangentPropagation" : true});
        }
        {
            var Q0;
            Q0=makeQuery(id+"F27.opExtrude","CAP_FACE",FACE,{"disambiguationData":[OSD([sQuery(id+"F26.wireOp",EDGE,"E59.bottom"),sQuery(id+"F26.wireOp",EDGE,"E59.top"),sQuery(id+"F26.wireOp",EDGE,"E59.left"),sQuery(id+"F26.wireOp",EDGE,"E59.right"),sQuery(id+"F26.wireOp",EDGE,"E60.filletArc"),sQuery(id+"F26.wireOp",EDGE,"E61.filletArc")])],"isStart":false});
            var sketch = newSketch(context, id + "F29", { "sketchPlane" : qUnion([Q0])});
            skCircle(sketch, "E62", {"center": v(565.83, 802.25) * mm, "radius": 17.78 * mm});
            skPoint(sketch, "E62.centerSnap0", {"position": v(594.26, 802.25) * mm});
            skLineSegment(sketch, "E63.bottom", {"start": v(565.83, 802.25) * mm, "end": v(565.68, 802.25) * mm});
            skLineSegment(sketch, "E63.top", {"start": v(565.83, 786.48) * mm, "end": v(565.68, 786.48) * mm});
            skLineSegment(sketch, "E63.right", {"start": v(565.68, 802.25) * mm, "end": v(565.68, 786.48) * mm});
            skLineSegment(sketch, "E64.MirrorCS", {"start": v(565.98, 802.25) * mm, "end": v(565.98, 786.48) * mm});
            skLineSegment(sketch, "E65.MirrorCS", {"start": v(565.83, 802.25) * mm, "end": v(565.98, 802.25) * mm});
            skLineSegment(sketch, "E66.MirrorCS", {"start": v(565.83, 786.48) * mm, "end": v(565.98, 786.48) * mm});
            skSolve(sketch);
        }
        {
            var Q0;
            Q0 = qSketchRegion(id + "F29", true);
            extrude(context, id + "F30", {"entities" : qUnion([Q0]), "operationType" : NewBodyOperationType.ADD, "depth" : 0.18 * mm, "offsetDistance" : 25.4 * mm});
        }
        {
            var Q0;
            Q0=makeQuery(id+"F30.opExtrude","CAP_EDGE",EDGE,{"disambiguationData":[OSD([sQuery(id+"F29.wireOp",EDGE,"E62")])],"isStart":false});
            chamfer(context, id + "F31", {"entities" : qUnion([Q0]), "width" : 0.1 * mm, "tangentPropagation" : true});
        }
        {
            var Q0;
            Q0=qCreatedBy(id+"F4.planeOp",FACE);
            var sketch = newSketch(context, id + "F32", { "sketchPlane" : qUnion([Q0])});
            skLineSegment(sketch, "E67.bottom", {"start": v(-214.54, -36.3) * mm, "end": v(686.98, -36.3) * mm});
            skLineSegment(sketch, "E67.top", {"start": v(-214.54, 2152.82) * mm, "end": v(686.98, 2152.82) * mm});
            skLineSegment(sketch, "E67.left", {"start": v(-214.54, -36.3) * mm, "end": v(-214.54, 2152.82) * mm});
            skLineSegment(sketch, "E67.right", {"start": v(686.98, -36.3) * mm, "end": v(686.98, 2152.82) * mm});
            skSolve(sketch);
        }
        {
            var Q0;
            Q0 = qSketchRegion(id + "F32", true);
            extrude(context, id + "F33", {"entities" : qUnion([Q0]), "operationType" : NewBodyOperationType.REMOVE, "oppositeDirection" : true, "depth" : 381 * mm, "offsetDistance" : 25.4 * mm});
        }
        {
            var Q0;
            Q0=makeQuery(id+"F1.opExtrude","SWEPT_BODY",BODY,{"disambiguationData":[OSD([sQuery(id+"F0.wireOp",EDGE,"E0.bottom"),sQuery(id+"F0.wireOp",EDGE,"E0.left"),sQuery(id+"F0.wireOp",EDGE,"E0.right"),sQuery(id+"F0.wireOp",EDGE,"E1")])]});
            var Q1;
            Q1=makeQuery(id+"F33.boolean.opBoolean","COPY",FACE,{"derivedFrom":makeQuery(id+"F33.opExtrude","CAP_FACE",FACE,{"disambiguationData":[OSD([sQuery(id+"F32.wireOp",EDGE,"E67.bottom"),sQuery(id+"F32.wireOp",EDGE,"E67.top"),sQuery(id+"F32.wireOp",EDGE,"E67.left"),sQuery(id+"F32.wireOp",EDGE,"E67.right")])],"isStart":true})});
            mirror(context, id + "F34", {"operationType" : NewBodyOperationType.ADD, "entities" : qUnion([Q0]), "mirrorPlane" : qUnion([Q1])});
        }
        {
            var Q0;
            {var subQ0=makeQuery(id+"F9.boolean.opBoolean","MERGE",FACE,{"derivedFrom":[makeQuery(id+"F6.boolean.opBoolean","MERGE",FACE,{"derivedFrom":[makeQuery(id+"F1.opExtrude","SWEPT_FACE",FACE,{"disambiguationData":[OSD([sQuery(id+"F0.wireOp",EDGE,"E0.right")])]}),makeQuery(id+"F6.opExtrude","SWEPT_FACE",FACE,{"disambiguationData":[OSD([sQuery(id+"F5.wireOp",EDGE,"E10.right")])]}),makeQuery(id+"F6.opExtrude","SWEPT_FACE",FACE,{"disambiguationData":[OSD([sQuery(id+"F5.wireOp",EDGE,"E11.right")])]})]}),makeQuery(id+"F9.opExtrude","SWEPT_FACE",FACE,{"disambiguationData":[OSD([sQuery(id+"F8.wireOp",EDGE,"E12.left")])]})]});Q0=makeQuery(id+"F34.boolean.opBoolean","MERGE",FACE,{"derivedFrom":[subQ0,makeQuery(id+"F34.opPattern","COPY",FACE,{"derivedFrom":subQ0,"instanceName":"1"})]});}
            var sketch = newSketch(context, id + "F35", { "sketchPlane" : qUnion([Q0])});
            skLineSegment(sketch, "E68.bottom", {"start": v(-204.71, 2173.14) * mm, "end": v(111.19, 2173.14) * mm});
            skLineSegment(sketch, "E68.top", {"start": v(-204.71, 0) * mm, "end": v(111.19, 0) * mm});
            skLineSegment(sketch, "E68.left", {"start": v(-204.71, 2173.14) * mm, "end": v(-204.71, 0) * mm});
            skLineSegment(sketch, "E68.right", {"start": v(111.19, 2173.14) * mm, "end": v(111.19, 0) * mm});
            skSolve(sketch);
        }
        {
            var Q0;
            Q0 = qSketchRegion(id + "F35", true);
            extrude(context, id + "F36", {"entities" : qUnion([Q0]), "operationType" : NewBodyOperationType.REMOVE, "oppositeDirection" : true, "depth" : 1 * mm, "offsetDistance" : 25.4 * mm});
        }
        {
            var Q0;
            Q0=qCreatedBy(makeId("Right.planeOp"),FACE);
            cPlane(context, id + "F37", {"entities" : qUnion([Q0]), "cplaneType" : CPlaneType.OFFSET, "offset" : 609.85 * mm, "width" : 152.4 * mm, "height" : 152.4 * mm});
        }
        {
            var Q0;
            Q0=makeQuery(id+"F1.opExtrude","SWEPT_BODY",BODY,{"disambiguationData":[OSD([sQuery(id+"F0.wireOp",EDGE,"E0.bottom"),sQuery(id+"F0.wireOp",EDGE,"E0.left"),sQuery(id+"F0.wireOp",EDGE,"E0.right"),sQuery(id+"F0.wireOp",EDGE,"E1")])]});
            var Q1;
            Q1=qCreatedBy(id+"F37.planeOp",FACE);
            mirror(context, id + "F38", {"entities" : qUnion([Q0]), "mirrorPlane" : qUnion([Q1])});
        }
        {
            var Q0;
            Q0=qCreatedBy(id+"F4.planeOp",FACE);
            var sketch = newSketch(context, id + "F39", { "sketchPlane" : qUnion([Q0])});
            skLineSegment(sketch, "E69", {"start": v(0, 0) * mm, "end": v(0, 1524) * mm});
            skArc(sketch, "E70", {"start": v(609.87, 2133.6) * mm, "mid": v(178.64, 1955.15) * mm, "end": v(0, 1524) * mm});
            skLineSegment(sketch, "E71", {"start": v(609.87, 2316.61) * mm, "end": v(-369.37, 2316.61) * mm});
            skLineSegment(sketch, "E72", {"start": v(-369.37, 2316.61) * mm, "end": v(-369.37, 1931.17) * mm});
            skLineSegment(sketch, "E73", {"start": v(-369.37, 1931.17) * mm, "end": v(-232.6, 1931.17) * mm});
            skLineSegment(sketch, "E74", {"start": v(-232.6, 1931.17) * mm, "end": v(-232.6, 0) * mm});
            skLineSegment(sketch, "E75", {"start": v(-232.6, 0) * mm, "end": v(0, 0) * mm});
            skLineSegment(sketch, "E76.MirrorCS", {"start": v(609.87, 2316.61) * mm, "end": v(1589.1, 2316.61) * mm});
            skArc(sketch, "E77.MirrorCS", {"start": v(609.87, 2133.6) * mm, "mid": v(1041.1, 1955.15) * mm, "end": v(1219.74, 1524) * mm});
            skLineSegment(sketch, "E78.MirrorCS", {"start": v(1219.74, 0) * mm, "end": v(1219.74, 1524) * mm});
            skLineSegment(sketch, "E79.MirrorCS", {"start": v(1452.34, 0) * mm, "end": v(1219.74, 0) * mm});
            skLineSegment(sketch, "E80.MirrorCS", {"start": v(1452.34, 1931.17) * mm, "end": v(1452.34, 0) * mm});
            skLineSegment(sketch, "E81.MirrorCS", {"start": v(1589.1, 1931.17) * mm, "end": v(1452.34, 1931.17) * mm});
            skLineSegment(sketch, "E82.MirrorCS", {"start": v(1589.1, 2316.61) * mm, "end": v(1589.1, 1931.17) * mm});
            skSolve(sketch);
        }
        {
            var Q0;
            Q0 = qSketchRegion(id + "F39", true);
            extrude(context, id + "F40", {"entities" : qUnion([Q0]), "depth" : 127 * mm, "offsetDistance" : 25.4 * mm});
        }
        {
            var Q0;
            Q0=makeQuery(id+"F40.opExtrude","CAP_FACE",FACE,{"disambiguationData":[OSD([sQuery(id+"F39.wireOp",EDGE,"E69"),sQuery(id+"F39.wireOp",EDGE,"E70"),sQuery(id+"F39.wireOp",EDGE,"E71"),sQuery(id+"F39.wireOp",EDGE,"E72"),sQuery(id+"F39.wireOp",EDGE,"E73"),sQuery(id+"F39.wireOp",EDGE,"E74"),sQuery(id+"F39.wireOp",EDGE,"E75"),sQuery(id+"F39.wireOp",EDGE,"E76.MirrorCS"),sQuery(id+"F39.wireOp",EDGE,"E77.MirrorCS"),sQuery(id+"F39.wireOp",EDGE,"E78.MirrorCS"),sQuery(id+"F39.wireOp",EDGE,"E79.MirrorCS"),sQuery(id+"F39.wireOp",EDGE,"E80.MirrorCS"),sQuery(id+"F39.wireOp",EDGE,"E81.MirrorCS"),sQuery(id+"F39.wireOp",EDGE,"E82.MirrorCS")])],"isStart":false});
            var sketch = newSketch(context, id + "F41", { "sketchPlane" : qUnion([Q0])});
            skArc(sketch, "E83", {"start": v(-232.6, 1931.17) * mm, "mid": v(-270, 2053.32) * mm, "end": v(-369.37, 2133.6) * mm});
            skLineSegment(sketch, "E84", {"start": v(-369.37, 2133.6) * mm, "end": v(-383.5, 1906.41) * mm});
            skLineSegment(sketch, "E85", {"start": v(-383.5, 1906.41) * mm, "end": v(-232.6, 1931.17) * mm});
            skArc(sketch, "E86.MirrorCS", {"start": v(1452.34, 1931.17) * mm, "mid": v(1489.73, 2053.32) * mm, "end": v(1589.1, 2133.6) * mm});
            skLineSegment(sketch, "E87.MirrorCS", {"start": v(1589.1, 2133.6) * mm, "end": v(1603.24, 1906.41) * mm});
            skLineSegment(sketch, "E88.MirrorCS", {"start": v(1603.24, 1906.41) * mm, "end": v(1452.34, 1931.17) * mm});
            skSolve(sketch);
        }
        {
            var Q0;
            Q0 = qSketchRegion(id + "F41", true);
            extrude(context, id + "F42", {"entities" : qUnion([Q0]), "operationType" : NewBodyOperationType.REMOVE, "oppositeDirection" : true, "depth" : 281.94 * mm, "offsetDistance" : 25.4 * mm});
        }
    });
